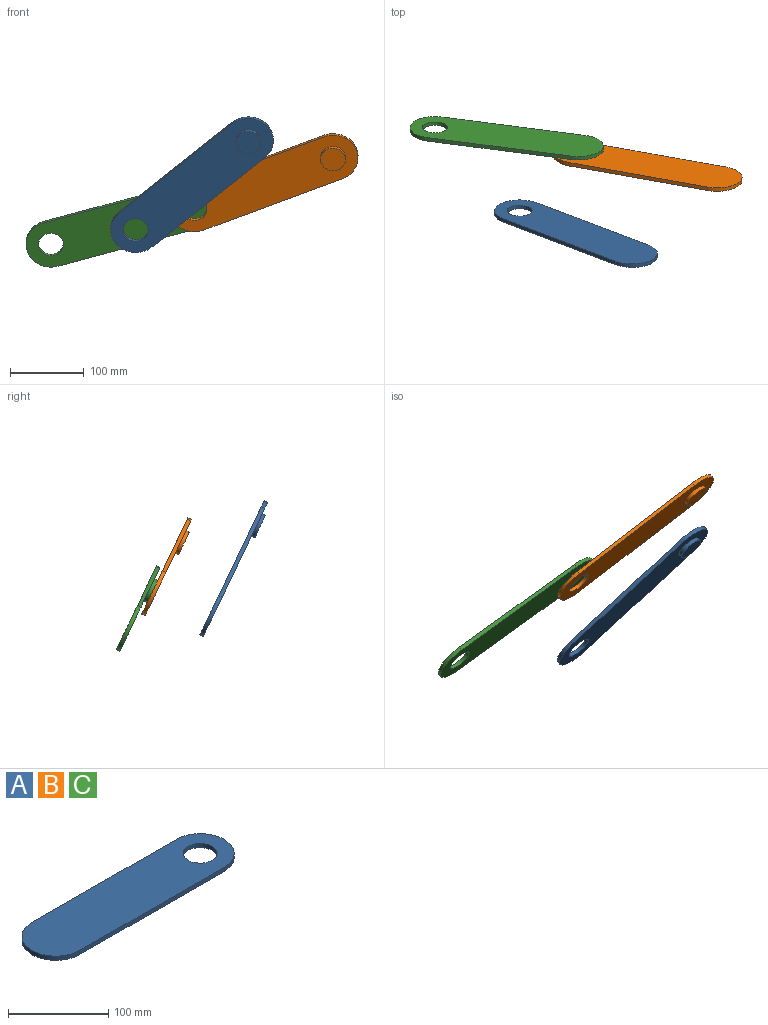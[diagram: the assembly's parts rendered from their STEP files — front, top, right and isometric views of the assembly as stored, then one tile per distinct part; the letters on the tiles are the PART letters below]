
ASSEMBLY  parts=3 mates=1
PART A: 9 faces, bbox 270.9x67.7x10.2 mm
  f0: plane 203.2x5.08mm, normal (0,-1,0), area 1032.3mm2, adj f1,f3,f4,f5
  f1: cylinder r=33.87mm len=67.73mm, axis (0,0,-1), area 540.5mm2, adj f0,f2,f4,f5
  f2: plane 203.2x5.08mm, normal (0,1,0), area 1032.3mm2, adj f1,f3,f4,f5
  f3: cylinder r=33.87mm len=67.73mm, axis (0,0,-1), area 540.5mm2, adj f0,f2,f4,f5
  f4: plane 270.93x67.73mm, normal (0,0,1), area 16465.9mm2, adj f0,f1,f2,f3,f8
  f5: plane 270.93x67.73mm, normal (0,0,-1), area 15565mm2, adj f0,f1,f2,f3,f6,f8
  f6: cylinder r=16.93mm len=33.87mm, axis (0,0,1), area 540.5mm2, adj f5,f7
  f7: plane 33.87x33.87mm, normal (0,0,-1), area 900.8mm2, adj f6
  f8: cylinder r=16.93mm len=33.87mm, axis (0,0,-1), area 540.5mm2, adj f4,f5
PART B: same geometry as A
PART C: same geometry as A
PLACE A rot(axis=(-0.2,0.52,0.83),145.3deg) t=(-277.69,97.35,-2.08)mm
PLACE B rot(axis=(-0.1,0.53,0.84),161.1deg) t=(-176.71,187.26,2.98)mm
PLACE C rot(axis=(-0.08,0.53,0.84),165.9deg) t=(-366.79,225.45,-53.19)mm
MATE revolute C.f3 <-> B.f1  axis (0,-0.9,-0.43) through (-264.78,213.86,-40.77)mm
